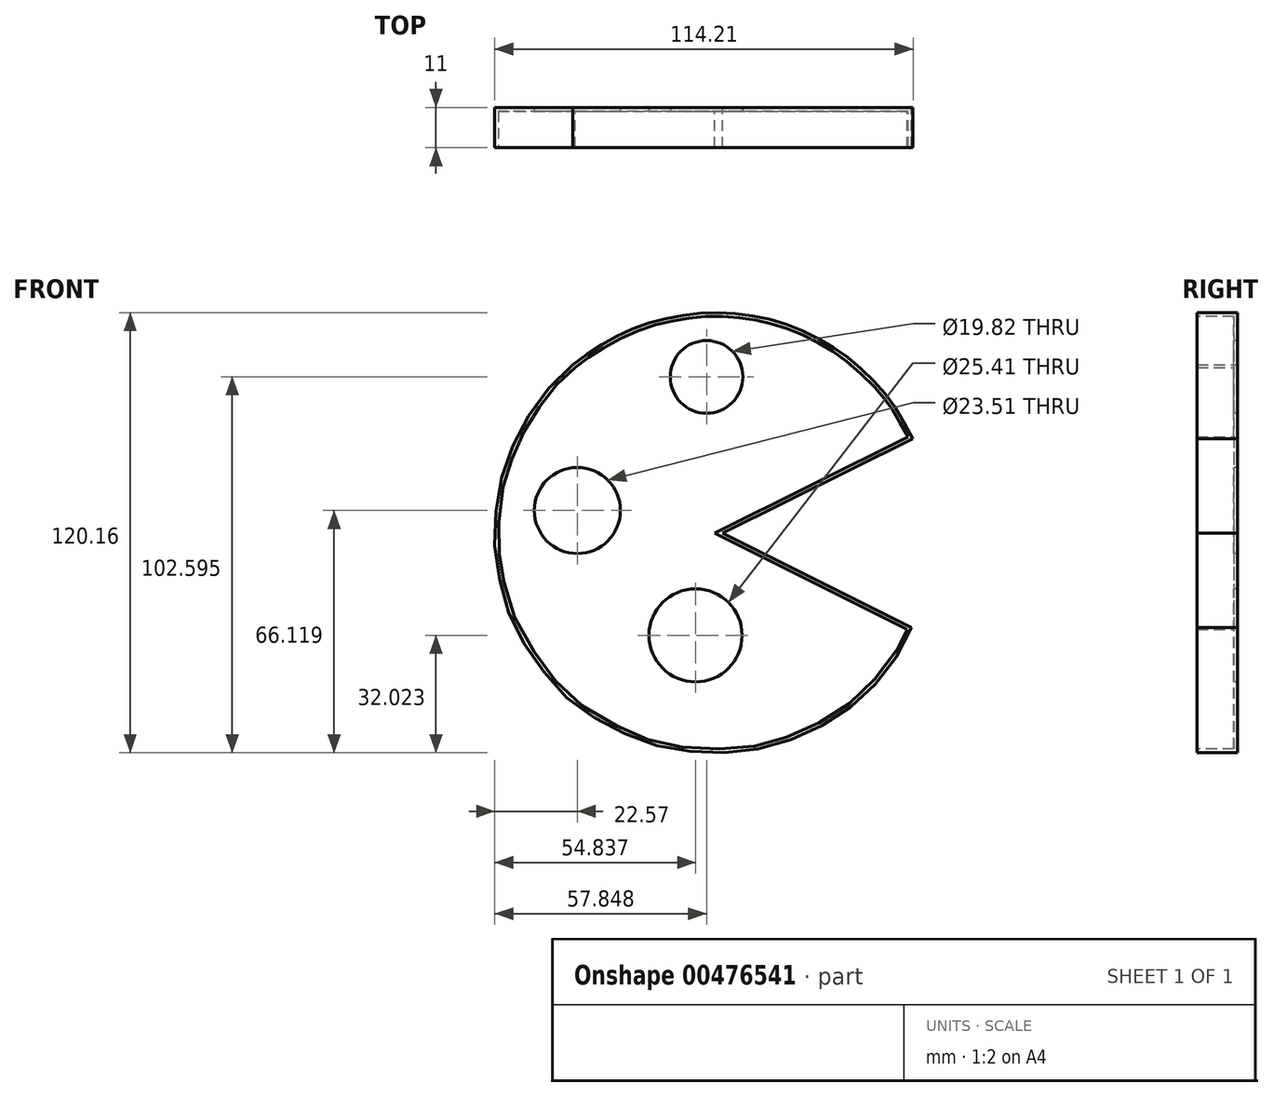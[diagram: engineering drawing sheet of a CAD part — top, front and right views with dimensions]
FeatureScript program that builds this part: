
annotation { "Feature Type Name" : "Feature", "Feature Type Description" : "" }
export const myFeature = defineFeature(function(context is Context, id is Id, definition is map)
    precondition{}
    {
        {
            var Q0;
            Q0=qCreatedBy(makeId("Front.planeOp"),FACE);
            var sketch = newSketch(context, id + "F0", { "sketchPlane" : qUnion([Q0])});
            skLineSegment(sketch, "E0", {"start": v(60.87, 30.25) * mm, "end": v(8.06, 4) * mm});
            skLineSegment(sketch, "E1", {"start": v(8.06, 4) * mm, "end": v(60.62, -22.36) * mm});
            skFitSpline(sketch, "E2", {"points": [v(60.87, 30.25) * mm, v(56.7, 37.55) * mm, v(52.8, 42.66) * mm, v(44.4, 50.64) * mm, v(36.22, 56.03) * mm, v(26.99, 60.18) * mm, v(18.63, 62.22) * mm, v(8.96, 63.21) * mm, v(-0.58, 62.4) * mm, v(-10.36, 60.18) * mm, v(-21.64, 54.97) * mm, v(-30.06, 49.21) * mm], "startDerivative": vector(-50.4, 91.9) * mm, "endDerivative": vector(-84.95, -62.8) * mm});
            skFitSpline(sketch, "E3", {"points": [v(-30.06, 49.21) * mm, v(-34.79, 44.74) * mm, v(-39.7, 38.57) * mm, v(-44.38, 30.98) * mm, v(-47.88, 22.73) * mm, v(-50.18, 13.65) * mm, v(-50.93, 0.71) * mm, v(-50.03, -6.58) * mm, v(-46.54, -18.96) * mm, v(-38.63, -32.11) * mm, v(-30.06, -41.58) * mm, v(-16.68, -49.6) * mm, v(-5.93, -53.52) * mm, v(7.96, -54.95) * mm, v(20.53, -53.85) * mm, v(31.36, -50.35) * mm, v(43.4, -43.68) * mm, v(52.36, -35.15) * mm, v(59.8, -24.65) * mm, v(60.62, -22.36) * mm], "startDerivative": vector(-116.37, -103.06) * mm, "endDerivative": vector(17.6, 74.95) * mm});
            skSolve(sketch);
        }
        {
            var Q0;
            Q0=makeQuery(id+"F0.imprint","IMPRINT",FACE,{"disambiguationData":[TD([[makeQuery(id+"F0.imprint","IMPRINT",EDGE,{"derivedFrom":sQuery(id+"F0.wireOp",EDGE,"E0")}),-1.0]])]});
            extrude(context, id + "F1", {"entities" : qUnion([Q0]), "depth" : 10 * mm});
        }
        {
            var Q0;
            Q0=makeQuery(id+"F1.opExtrude","CAP_FACE",FACE,{"disambiguationData":[OSD([sQuery(id+"F0.wireOp",EDGE,"E0"),sQuery(id+"F0.wireOp",EDGE,"E1"),sQuery(id+"F0.wireOp",EDGE,"E2"),sQuery(id+"F0.wireOp",EDGE,"E3")])],"isStart":false});
            shell(context, id + "F2", {"entities" : qUnion([Q0]), "thickness" : 1 * mm, "oppositeDirection" : true});
        }
        {
            var Q0;
            Q0=makeQuery(id+"F2.opShell","OFFSET_FACE",FACE,{"disambiguationData":[OSD([sQuery(id+"F0.wireOp",EDGE,"E0"),sQuery(id+"F0.wireOp",EDGE,"E1"),sQuery(id+"F0.wireOp",EDGE,"E2"),sQuery(id+"F0.wireOp",EDGE,"E3")])]});
            var sketch = newSketch(context, id + "F3", { "sketchPlane" : qUnion([Q0])});
            skCircle(sketch, "E4", {"center": v(5.89, 46.64) * mm, "radius": 9.91 * mm});
            skCircle(sketch, "E5", {"center": v(-29.4, 10.17) * mm, "radius": 11.76 * mm});
            skCircle(sketch, "E6", {"center": v(2.88, -23.93) * mm, "radius": 12.7 * mm});
            skSolve(sketch);
        }
        {
            var Q0;
            Q0=makeQuery(id+"F3.imprint","IMPRINT",FACE,{"disambiguationData":[TD([[makeQuery(id+"F3.imprint","IMPRINT",EDGE,{"derivedFrom":sQuery(id+"F3.wireOp",EDGE,"E4")}),1.0]])]});
            extrude(context, id + "F4", {"entities" : qUnion([Q0]), "operationType" : NewBodyOperationType.REMOVE, "oppositeDirection" : true, "depth" : 25 * mm});
        }
        {
            var Q0;
            Q0=makeQuery(id+"F3.imprint","IMPRINT",FACE,{"disambiguationData":[TD([[makeQuery(id+"F3.imprint","IMPRINT",EDGE,{"derivedFrom":sQuery(id+"F3.wireOp",EDGE,"E5")}),1.0]])]});
            var Q1;
            Q1=makeQuery(id+"F3.imprint","IMPRINT",FACE,{"disambiguationData":[TD([[makeQuery(id+"F3.imprint","IMPRINT",EDGE,{"derivedFrom":sQuery(id+"F3.wireOp",EDGE,"E6")}),1.0]])]});
            extrude(context, id + "F5", {"entities" : qUnion([Q0, Q1]), "operationType" : NewBodyOperationType.REMOVE, "oppositeDirection" : true, "depth" : 25 * mm});
        }
    });
